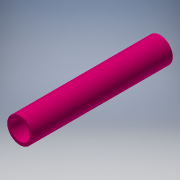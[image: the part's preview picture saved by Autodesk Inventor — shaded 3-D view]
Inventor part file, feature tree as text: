
AUTODESK INVENTOR PART (.ipt)
format: ipt  version: 2018.2 (Build 222227000, 227)  size: 109,056 bytes
history: native  units: in
note: dims shown in document units (in); Inventor stores cm internally (conversion verified against a paired STEP export)
features: extrude x1, sketch x1
ambient origin geometry x8: Origin, YZ Plane, XZ Plane, XY Plane, X Axis, Y Axis, Z Axis, Center Point
bodies: Solid1 (feature_tree)
feature tree (2):
  extrude  "Extrusion1"  Depth=7.25in
  sketch  "Sketch1"  dims[d0=1.315in d1=1.0in d2=7.25in d3=0.0in]
